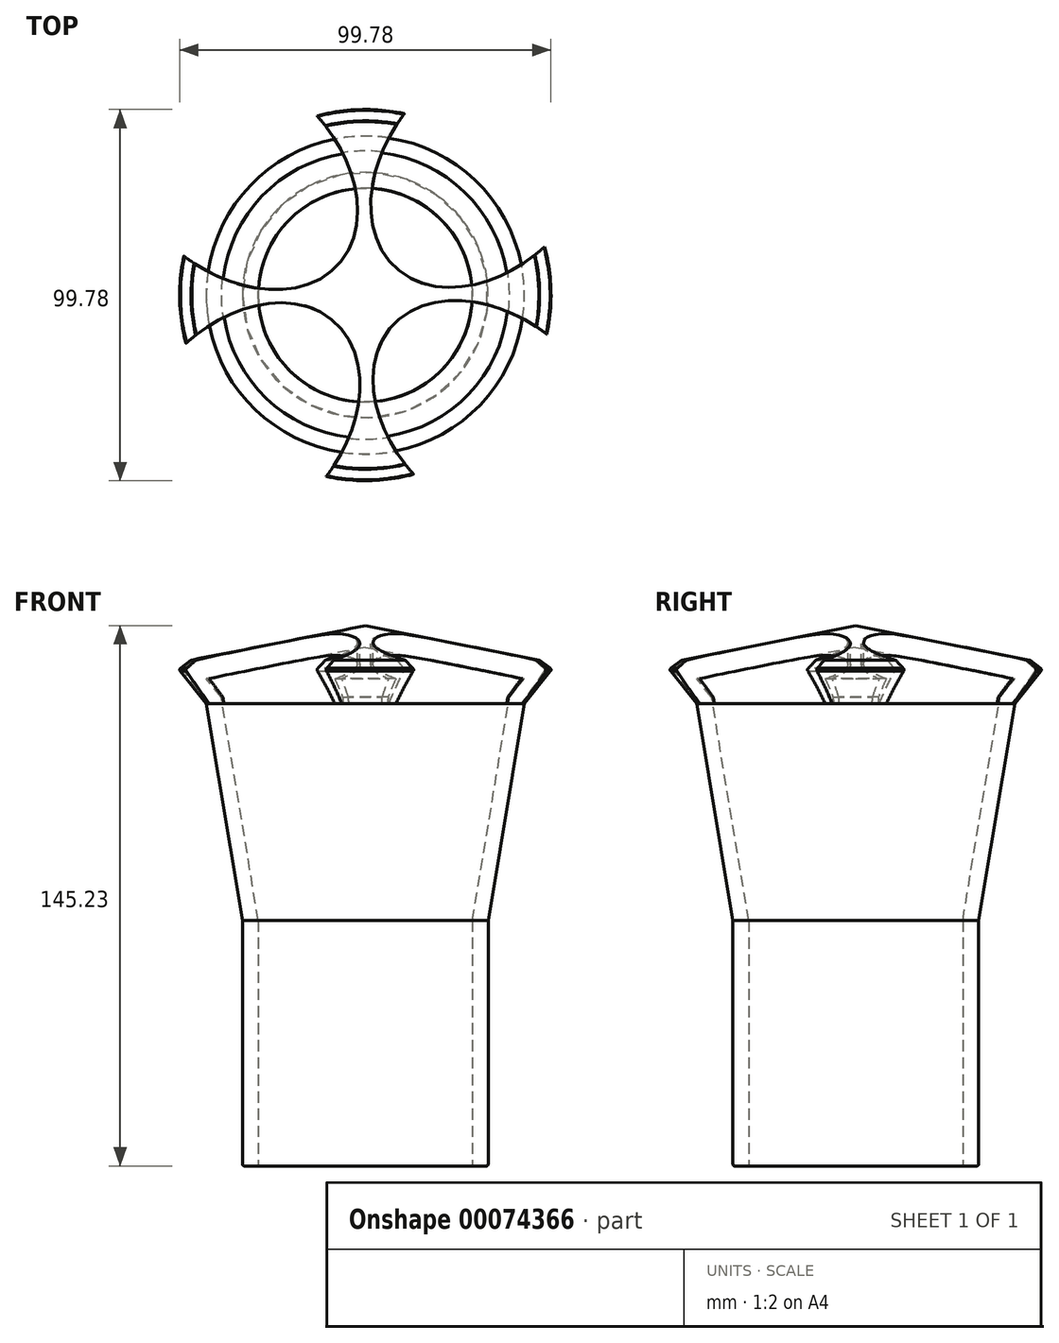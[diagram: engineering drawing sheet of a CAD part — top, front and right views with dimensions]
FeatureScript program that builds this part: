
annotation { "Feature Type Name" : "Feature", "Feature Type Description" : "" }
export const myFeature = defineFeature(function(context is Context, id is Id, definition is map)
    precondition{}
    {
        {
            var Q0;
            Q0=qCreatedBy(makeId("Front.planeOp"),FACE);
            var sketch = newSketch(context, id + "F0", { "sketchPlane" : qUnion([Q0])});
            skLineSegment(sketch, "E0", {"start": v(28.74, 40.5) * mm, "end": v(38.74, 100.5) * mm});
            skLineSegment(sketch, "E1", {"start": v(38.74, 100.5) * mm, "end": v(42.74, 105.5) * mm});
            skLineSegment(sketch, "E2.0", {"start": v(42.7, 98.73) * mm, "end": v(50.07, 107.94) * mm});
            skLineSegment(sketch, "E2.1", {"start": v(33, 40.5) * mm, "end": v(42.7, 98.73) * mm});
            skLineSegment(sketch, "E3", {"start": v(46.74, 110.5) * mm, "end": v(50.07, 107.94) * mm});
            skLineSegment(sketch, "E4", {"start": v(28.74, 40.5) * mm, "end": v(33, 40.5) * mm});
            skLineSegment(sketch, "E5", {"start": v(0, 0) * mm, "end": v(0, 71.44) * mm, "construction": true});
            skLineSegment(sketch, "E6", {"start": v(28.74, 40.5) * mm, "end": v(28.74, -25.5) * mm});
            skLineSegment(sketch, "E7", {"start": v(28.74, -25.5) * mm, "end": v(33, -25.5) * mm});
            skLineSegment(sketch, "E8", {"start": v(33, -25.5) * mm, "end": v(33, 40.5) * mm});
            skLineSegment(sketch, "E9", {"start": v(0, 119.73) * mm, "end": v(46.74, 110.5) * mm});
            skLineSegment(sketch, "E10", {"start": v(0, 119.73) * mm, "end": v(0, 113.92) * mm});
            skLineSegment(sketch, "E11", {"start": v(0, 113.92) * mm, "end": v(42.74, 105.5) * mm});
            skSolve(sketch);
        }
        {
            var Q0;
            Q0=makeQuery(id+"F0.imprint","IMPRINT",FACE,{"disambiguationData":[TD([[makeQuery(id+"F0.imprint","IMPRINT",EDGE,{"derivedFrom":sQuery(id+"F0.wireOp",EDGE,"E0")}),-1.0]])]});
            var Q1;
            Q1=makeQuery(id+"F0.imprint","IMPRINT",FACE,{"disambiguationData":[TD([[makeQuery(id+"F0.imprint","IMPRINT",EDGE,{"derivedFrom":sQuery(id+"F0.wireOp",EDGE,"E4")}),-1.0]])]});
            var Q2;
            Q2=sQuery(id+"F0.wireOp",EDGE,"E5");
            revolve(context, id + "F1", {"entities" : qUnion([Q0, Q1]), "axis" : qUnion([Q2]), "revolveType" : RevolveType.FULL});
        }
        {
            var Q0;
            Q0=sQuery(id+"F0.wireOp",VERTEX,"E2.0.start");
            var Q1;
            Q1=makeQuery(id+"F1.opRevolve","SWEPT_EDGE",EDGE,{"disambiguationData":[OSD([sQuery(id+"F0.wireOp",EDGE,"E2.0"),sQuery(id+"F0.wireOp",EDGE,"E2.1")])]});
            cPlane(context, id + "F2", {"entities" : qUnion([Q0, Q1]), "cplaneType" : CPlaneType.LINE_POINT, "offset" : 5 * mm, "width" : 150 * mm, "height" : 150 * mm});
        }
        {
            var Q0;
            Q0=makeQuery(id+"F1.opRevolve","SWEPT_EDGE",EDGE,{"disambiguationData":[OSD([sQuery(id+"F0.wireOp",EDGE,"E7"),sQuery(id+"F0.wireOp",EDGE,"E8")])]});
            var Q1;
            Q1=makeQuery(id+"F1.opRevolve","SWEPT_EDGE",EDGE,{"disambiguationData":[OSD([sQuery(id+"F0.wireOp",EDGE,"E6"),sQuery(id+"F0.wireOp",EDGE,"E7")])]});
            fillet(context, id + "F3", {"entities" : qUnion([Q0, Q1]), "radius" : 0.5 * mm, "tangentPropagation" : true, "rho" : 0.5, "crossSection" : FilletCrossSection.CONIC, "allowEdgeOverflow" : false});
        }
        {
            var Q0;
            Q0=makeQuery(id+"F1.opRevolve","SWEPT_FACE",FACE,{"disambiguationData":[OSD([sQuery(id+"F0.wireOp",EDGE,"E3")])]});
            fillet(context, id + "F4", {"entities" : qUnion([Q0]), "radius" : 0.5 * mm, "tangentPropagation" : true, "rho" : 0.5, "crossSection" : FilletCrossSection.CONIC, "allowEdgeOverflow" : false});
        }
        {
            var Q0;
            Q0=qCreatedBy(id+"F2.planeOp",FACE);
            var sketch = newSketch(context, id + "F5", { "sketchPlane" : qUnion([Q0])});
            skEllipse(sketch, "E12", {"center": v(-34.5, -32.67) * mm, "majorRadius": 36.6 * mm, "minorRadius": 26.22 * mm, "majorAxis": v(0.75, 0.66)});
            skEllipse(sketch, "E13.1.0", {"center": v(32.67, -34.5) * mm, "majorRadius": 36.6 * mm, "minorRadius": 26.22 * mm, "majorAxis": v(-0.66, 0.75)});
            skEllipse(sketch, "E13.2.0", {"center": v(34.5, 32.67) * mm, "majorRadius": 36.6 * mm, "minorRadius": 26.22 * mm, "majorAxis": v(-0.75, -0.66)});
            skEllipse(sketch, "E13.3.0", {"center": v(-32.67, 34.5) * mm, "majorRadius": 36.6 * mm, "minorRadius": 26.22 * mm, "majorAxis": v(0.66, -0.75)});
            skPoint(sketch, "E13.center", {"position": v(0, 0) * mm});
            skSolve(sketch);
        }
        {
            var Q0;
            Q0 = qSketchRegion(id + "F5", true);
            extrude(context, id + "F6", {"entities" : qUnion([Q0]), "operationType" : NewBodyOperationType.REMOVE, "endBound" : BoundingType.THROUGH_ALL, "oppositeDirection" : true, "depth" : 25 * mm});
        }
    });
